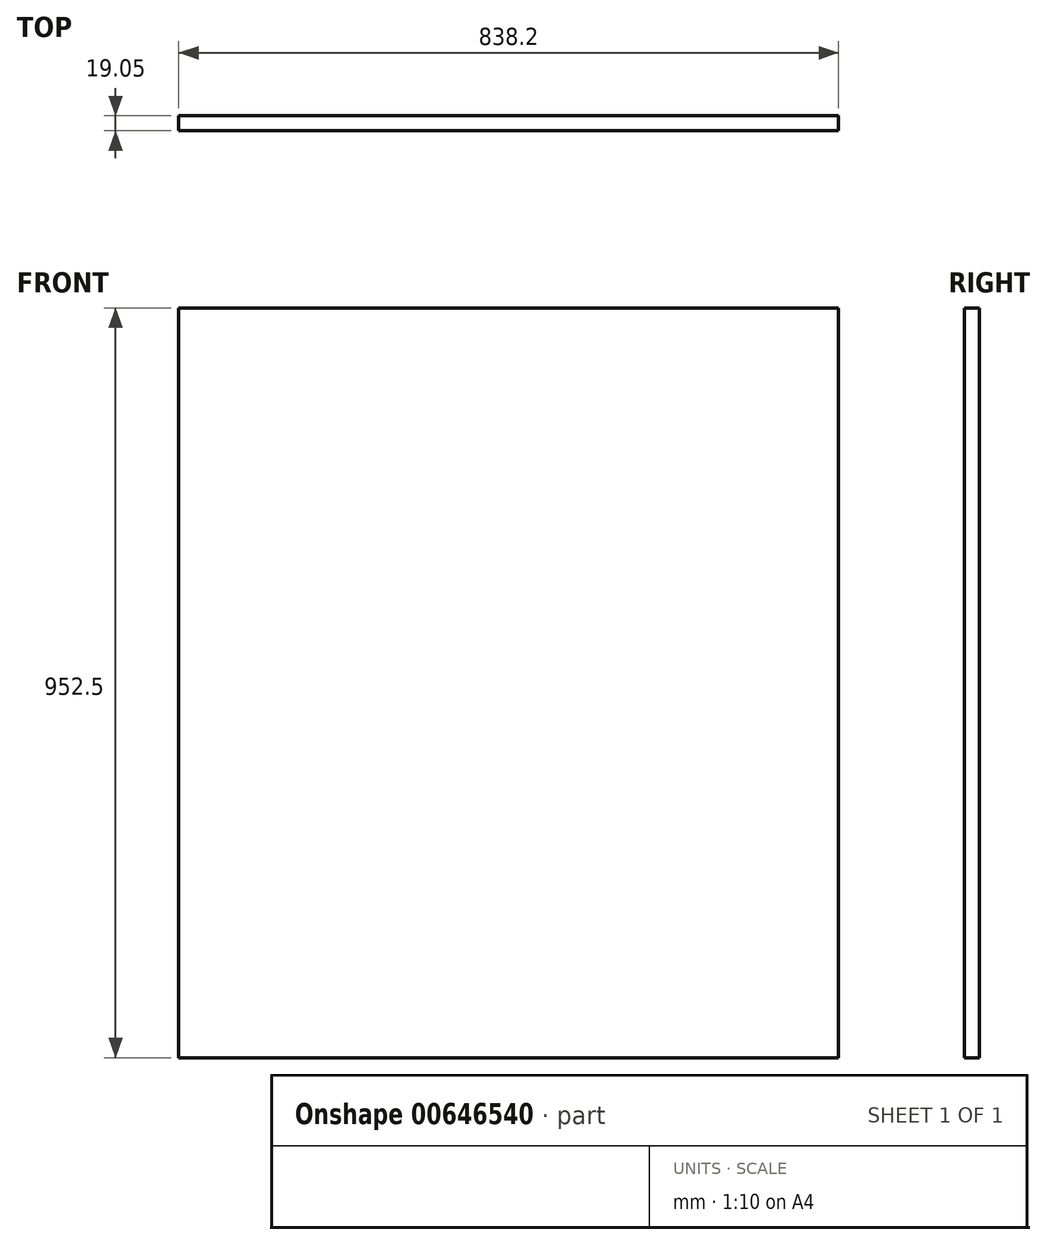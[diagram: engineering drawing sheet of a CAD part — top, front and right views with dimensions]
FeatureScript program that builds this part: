
annotation { "Feature Type Name" : "Feature", "Feature Type Description" : "" }
export const myFeature = defineFeature(function(context is Context, id is Id, definition is map)
    precondition{}
    {
        {
            var Q0;
            Q0=qCreatedBy(makeId("Front.planeOp"),FACE);
            var sketch = newSketch(context, id + "F0", { "sketchPlane" : qUnion([Q0])});
            skLineSegment(sketch, "E0.bottom", {"start": v(419.1, 476.25) * mm, "end": v(-419.1, 476.25) * mm});
            skLineSegment(sketch, "E0.top", {"start": v(419.1, -476.25) * mm, "end": v(-419.1, -476.25) * mm});
            skLineSegment(sketch, "E0.left", {"start": v(419.1, 476.25) * mm, "end": v(419.1, -476.25) * mm});
            skLineSegment(sketch, "E0.right", {"start": v(-419.1, 476.25) * mm, "end": v(-419.1, -476.25) * mm});
            skPoint(sketch, "E0.middle", {"position": v(0, 0) * mm});
            skSolve(sketch);
        }
        {
            var Q0;
            Q0=makeQuery(id+"F0.imprint","IMPRINT",FACE,{"disambiguationData":[TD([[makeQuery(id+"F0.imprint","IMPRINT",EDGE,{"derivedFrom":sQuery(id+"F0.wireOp",EDGE,"E0.bottom")}),1.0]])]});
            extrude(context, id + "F1", {"entities" : qUnion([Q0]), "depth" : 19.05 * mm, "offsetDistance" : 25.4 * mm});
        }
    });
